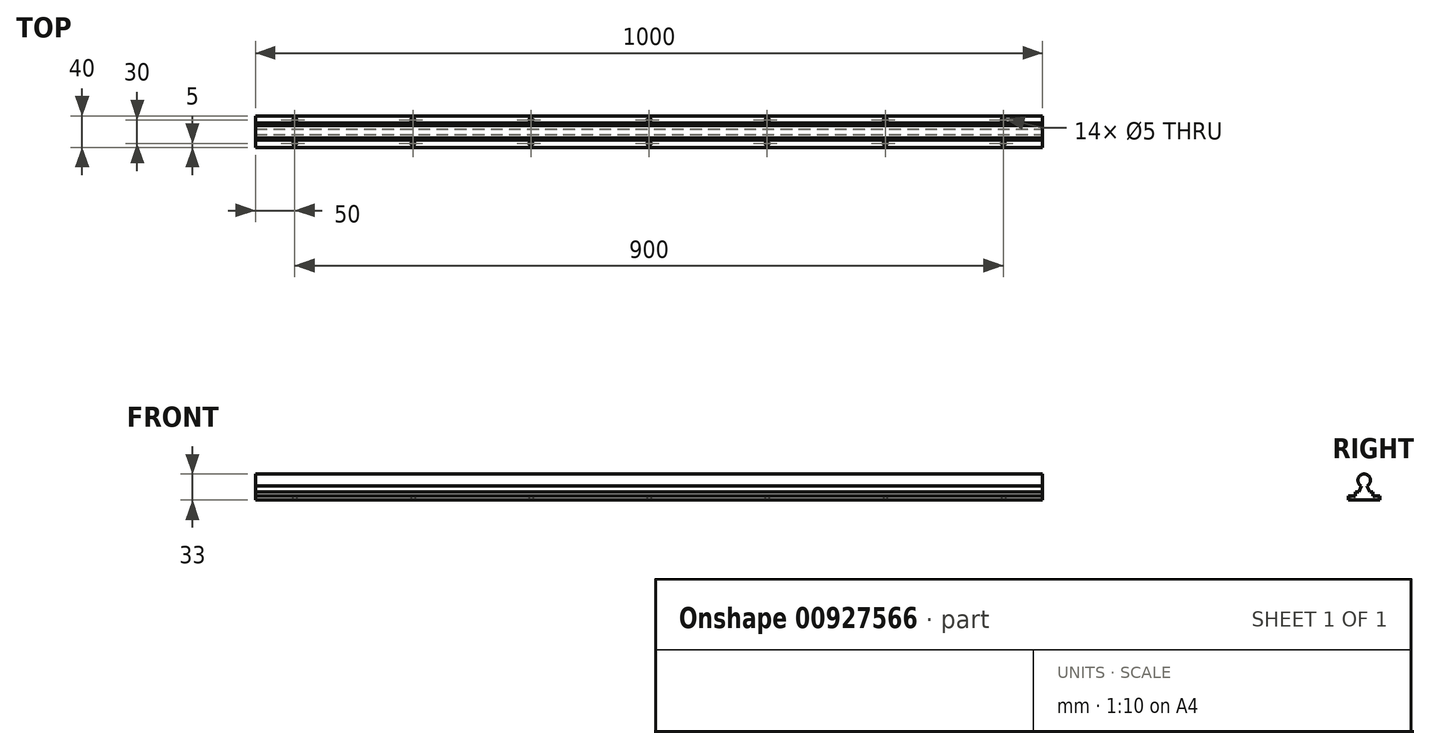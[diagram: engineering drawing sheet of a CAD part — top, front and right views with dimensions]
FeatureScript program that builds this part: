
annotation { "Feature Type Name" : "Feature", "Feature Type Description" : "" }
export const myFeature = defineFeature(function(context is Context, id is Id, definition is map)
    precondition{}
    {
        {
            var Q0;
            Q0=qCreatedBy(makeId("Right.planeOp"),FACE);
            var sketch = newSketch(context, id + "F0", { "sketchPlane" : qUnion([Q0])});
            skLineSegment(sketch, "E0", {"start": v(0, 0) * mm, "end": v(40, 0) * mm});
            skLineSegment(sketch, "E1", {"start": v(-29.14, 25) * mm, "end": v(79.88, 25) * mm, "construction": true});
            skLineSegment(sketch, "E2", {"start": v(40, 0) * mm, "end": v(40, 5) * mm});
            skLineSegment(sketch, "E3", {"start": v(0, 0) * mm, "end": v(0, 5) * mm});
            skLineSegment(sketch, "E4", {"start": v(20, 37.91) * mm, "end": v(20, -10.94) * mm, "construction": true});
            skPoint(sketch, "E4.startSnap0", {"position": v(20, 0) * mm});
            skLineSegment(sketch, "E5", {"start": v(5, 9.62) * mm, "end": v(5, -10) * mm, "construction": true});
            skLineSegment(sketch, "E6.MirrorCS", {"start": v(35, 9.62) * mm, "end": v(35, -10) * mm, "construction": true});
            skArc(sketch, "E7", {"start": v(23.47, 17.8) * mm, "mid": v(20, 33) * mm, "end": v(16.53, 17.8) * mm});
            skLineSegment(sketch, "E8", {"start": v(0, 5) * mm, "end": v(9, 5) * mm});
            skLineSegment(sketch, "E9", {"start": v(9, 10) * mm, "end": v(9, 5) * mm});
            skLineSegment(sketch, "E10", {"start": v(9, 10) * mm, "end": v(13, 10) * mm});
            skLineSegment(sketch, "E11", {"start": v(16.53, 17.8) * mm, "end": v(13, 10) * mm});
            skLineSegment(sketch, "E12.MirrorCS", {"start": v(23.47, 17.8) * mm, "end": v(27, 10) * mm});
            skLineSegment(sketch, "E13.MirrorCS", {"start": v(31, 10) * mm, "end": v(27, 10) * mm});
            skLineSegment(sketch, "E14.MirrorCS", {"start": v(31, 10) * mm, "end": v(31, 5) * mm});
            skLineSegment(sketch, "E15.MirrorCS", {"start": v(40, 5) * mm, "end": v(31, 5) * mm});
            skSolve(sketch);
        }
        {
            var Q0;
            Q0 = qSketchRegion(id + "F0", true);
            extrude(context, id + "F1", {"entities" : qUnion([Q0]), "oppositeDirection" : true, "depth" : 1000 * mm, "offsetDistance" : 25 * mm});
        }
        {
            var Q0;
            Q0=makeQuery(id+"F1.opExtrude","SWEPT_FACE",FACE,{"disambiguationData":[OSD([sQuery(id+"F0.wireOp",EDGE,"E0")])]});
            var sketch = newSketch(context, id + "F2", { "sketchPlane" : qUnion([Q0])});
            skLineSegment(sketch, "E16", {"start": v(-1181.44, -5) * mm, "end": v(213.21, -5) * mm, "construction": true});
            skLineSegment(sketch, "E17", {"start": v(-1185.27, -35) * mm, "end": v(232.34, -35) * mm, "construction": true});
            skCircle(sketch, "E18", {"center": v(-50, -5) * mm, "radius": 2.5 * mm});
            skCircle(sketch, "E19", {"center": v(-200, -5) * mm, "radius": 2.5 * mm});
            skCircle(sketch, "E20.1.0.0", {"center": v(-350, -5) * mm, "radius": 2.5 * mm});
            skCircle(sketch, "E20.2.0.0", {"center": v(-500, -5) * mm, "radius": 2.5 * mm});
            skCircle(sketch, "E20.3.0.0", {"center": v(-650, -5) * mm, "radius": 2.5 * mm});
            skCircle(sketch, "E20.4.0.0", {"center": v(-800, -5) * mm, "radius": 2.5 * mm});
            skCircle(sketch, "E20.5.0.0", {"center": v(-950, -5) * mm, "radius": 2.5 * mm});
            skLineSegment(sketch, "E20.direction1", {"start": v(-200, -5) * mm, "end": v(-350, -5) * mm, "construction": true});
            skLineSegment(sketch, "E21", {"start": v(-1082.11, -20) * mm, "end": v(132.39, -20) * mm, "construction": true});
            skPoint(sketch, "E21.endSnap0", {"position": v(0, -20) * mm});
            skCircle(sketch, "E22.MirrorC", {"center": v(-950, -35) * mm, "radius": 2.5 * mm});
            skCircle(sketch, "E23.MirrorC", {"center": v(-800, -35) * mm, "radius": 2.5 * mm});
            skCircle(sketch, "E24.MirrorC", {"center": v(-650, -35) * mm, "radius": 2.5 * mm});
            skCircle(sketch, "E25.MirrorC", {"center": v(-500, -35) * mm, "radius": 2.5 * mm});
            skCircle(sketch, "E26.MirrorC", {"center": v(-350, -35) * mm, "radius": 2.5 * mm});
            skCircle(sketch, "E27.MirrorC", {"center": v(-200, -35) * mm, "radius": 2.5 * mm});
            skCircle(sketch, "E28.MirrorC", {"center": v(-50, -35) * mm, "radius": 2.5 * mm});
            skSolve(sketch);
        }
        {
            var Q0;
            Q0 = qSketchRegion(id + "F2", true);
            extrude(context, id + "F3", {"entities" : qUnion([Q0]), "operationType" : NewBodyOperationType.REMOVE, "endBound" : BoundingType.THROUGH_ALL, "oppositeDirection" : true, "depth" : 25 * mm, "offsetDistance" : 25 * mm});
        }
    });
